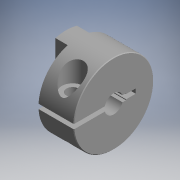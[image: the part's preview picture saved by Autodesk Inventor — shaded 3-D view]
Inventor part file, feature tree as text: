
AUTODESK INVENTOR PART (.ipt)
format: ipt  version: 2017.3 (Build 213256000, 256)  size: 174,080 bytes
history: native  units: mm (DEFAULTED — no unit token found)
features: other x14, sketch x8, extrude x4, revolve x2, hole x2
ambient origin geometry x8: Origin, YZ Plane, XZ Plane, XY Plane, X Axis, Y Axis, Z Axis, Center Point
bodies: Solid1 (feature_tree)
feature tree (30):
  revolve  "Revolution1"  [1 undecoded]
  extrude  "Extrusion1"  Depth=4.0mm TaperAngle=0.0deg
  revolve  "Revolution2"  [1 undecoded]
  hole  "Hole1"  [1 undecoded]
  extrude  "Extrusion2"  [1 undecoded]
  hole  "Hole2"  [1 undecoded]
  extrude  "Extrusion3"  [1 undecoded]
  extrude  "Extrusion4"  [1 undecoded]
  other  "L_XY"
  other  "L_YZ"
  other  "L_ZX"
  other  "L_X"
  other  "L_Y"
  other  "L_Z"
  other  "L_Center"
  other  "screw_XY"
  other  "screw_YZ"
  other  "screw_ZX"
  other  "screw_X"
  other  "screw_Y"
  other  "screw_Z"
  other  "screw_Center"
  sketch  "Sketch_1"  dims[d0=360.0deg d1=11.5mm d2=0.0mm]
  sketch  "Sketch_6"  dims[d13=13.0mm d14=6.0mm d15=4.0mm d16=2.0mm d17=90.0deg d18=4.0mm d19=0.0mm d20=31.0mm d21=0.0mm]
  sketch  "Sketch_7"
  sketch  "Sketch4"  dims[d4=3.242mm d5=7.05mm d6=4.0mm d7=2.0mm d8=90.0deg d9=12.25mm d10=0.0mm d11=4.0mm d12=0.0mm]
  sketch  "Sketch_2"  dims[d3=360.0deg]
  sketch  "Sketch6"  dims[d22=15.5mm d23=0.0mm d24=0.0mm]
  sketch  "Sketch_15"
  sketch  "Sketch_8"
note: 7 required parameter values undecoded (feature->parameter linkage not recoverable at this tier; creation-order binding heuristic only, values carry confidence <= 0.55)